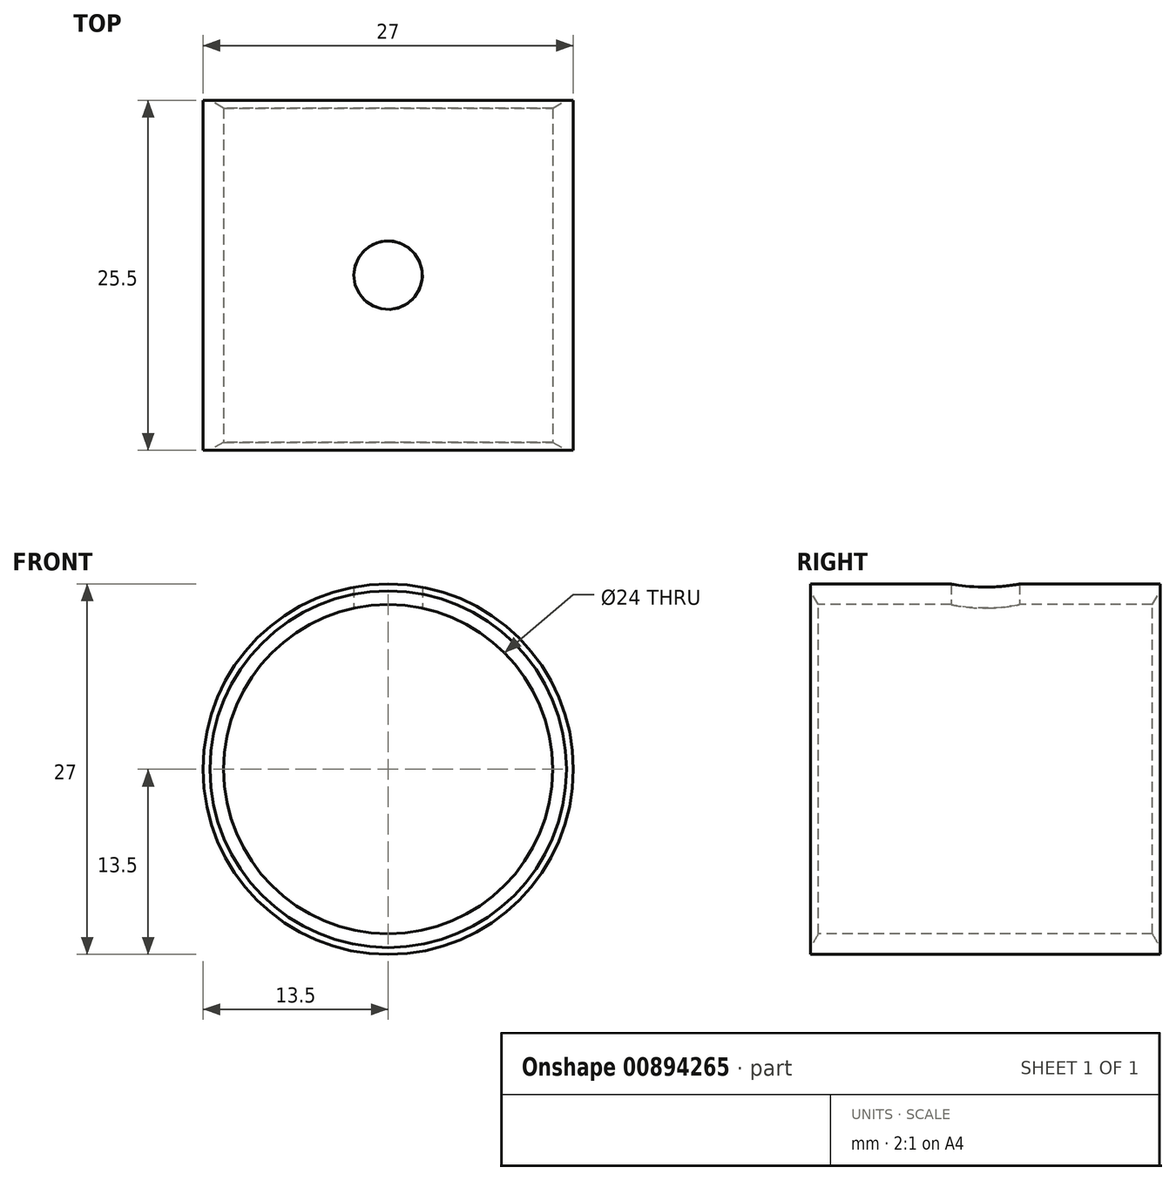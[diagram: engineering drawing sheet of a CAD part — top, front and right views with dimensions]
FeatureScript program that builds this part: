
annotation { "Feature Type Name" : "Feature", "Feature Type Description" : "" }
export const myFeature = defineFeature(function(context is Context, id is Id, definition is map)
    precondition{}
    {
        {
            var Q0;
            Q0=qCreatedBy(makeId("Front.planeOp"),FACE);
            var sketch = newSketch(context, id + "F0", { "sketchPlane" : qUnion([Q0])});
            skCircle(sketch, "E0", {"center": v(0, 0) * mm, "radius": 13.5 * mm});
            skCircle(sketch, "E1", {"center": v(0, 0) * mm, "radius": 12 * mm});
            skSolve(sketch);
        }
        {
            var Q0;
            Q0 = qSketchRegion(id + "F0", true);
            extrude(context, id + "F1", {"entities" : qUnion([Q0]), "oppositeDirection" : true, "depth" : 25.5 * mm, "offsetDistance" : 25 * mm, "symmetric" : true});
        }
        {
            var Q0;
            Q0=makeQuery(id+"F1.opExtrude","CAP_EDGE",EDGE,{"disambiguationData":[OSD([sQuery(id+"F0.wireOp",EDGE,"E1")])],"isStart":true});
            var Q1;
            Q1=makeQuery(id+"F1.opExtrude","CAP_EDGE",EDGE,{"disambiguationData":[OSD([sQuery(id+"F0.wireOp",EDGE,"E1")])],"isStart":false});
            chamfer(context, id + "F2", {"entities" : qUnion([Q0, Q1]), "chamferType" : ChamferType.OFFSET_ANGLE, "width" : 1 * mm, "oppositeDirection" : false, "angle" : 30 * degree, "tangentPropagation" : true});
        }
        {
            var Q0;
            Q0=qCreatedBy(makeId("Top.planeOp"),FACE);
            var sketch = newSketch(context, id + "F3", { "sketchPlane" : qUnion([Q0])});
            skCircle(sketch, "E2", {"center": v(0, 0) * mm, "radius": 2.5 * mm});
            skSolve(sketch);
        }
        {
            var Q0;
            Q0 = qSketchRegion(id + "F3", true);
            extrude(context, id + "F4", {"entities" : qUnion([Q0]), "operationType" : NewBodyOperationType.REMOVE, "endBound" : BoundingType.THROUGH_ALL, "depth" : 25 * mm, "offsetDistance" : 25 * mm});
        }
    });
